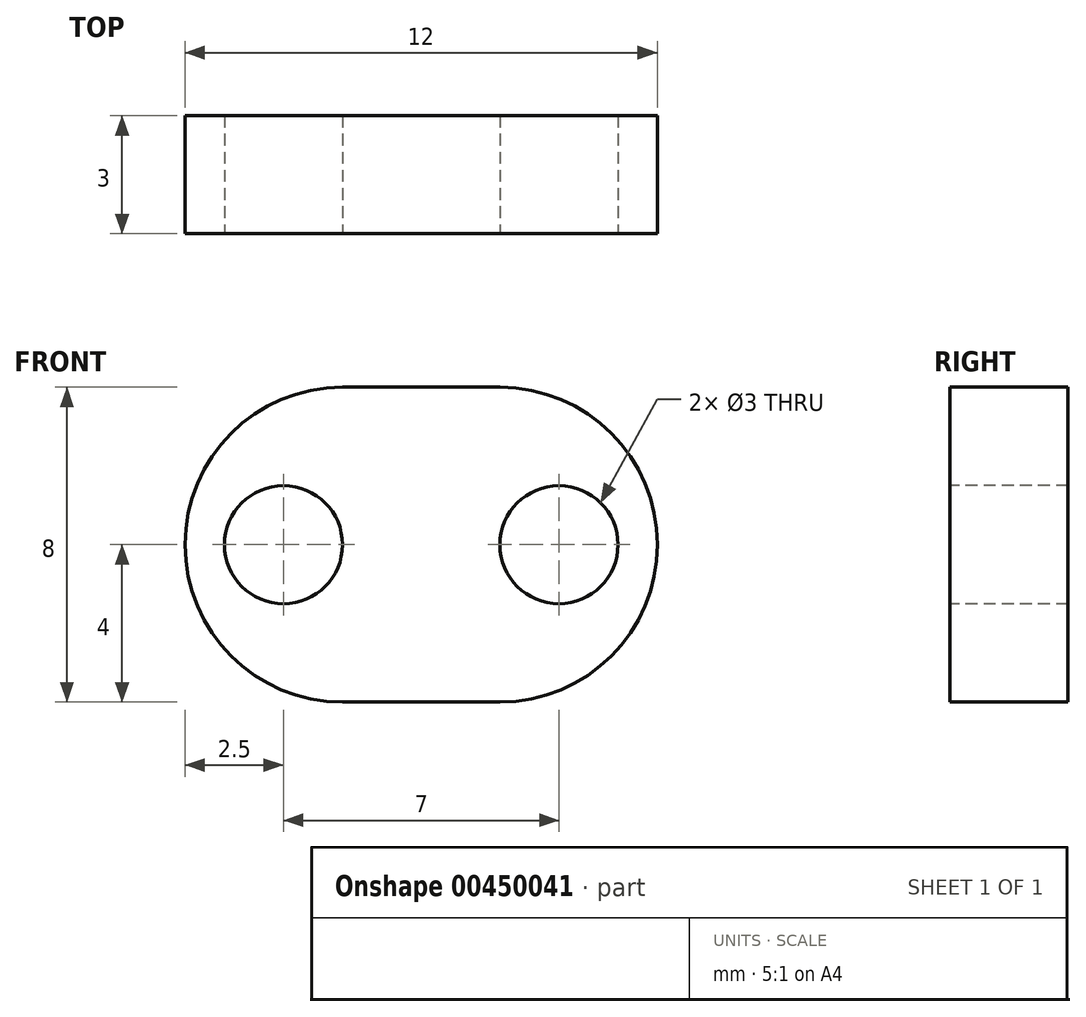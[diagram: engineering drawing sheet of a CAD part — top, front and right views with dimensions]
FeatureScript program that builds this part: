
annotation { "Feature Type Name" : "Feature", "Feature Type Description" : "" }
export const myFeature = defineFeature(function(context is Context, id is Id, definition is map)
    precondition{}
    {
        {
            var Q0;
            Q0=qCreatedBy(makeId("Top.planeOp"),FACE);
            var sketch = newSketch(context, id + "F0", { "sketchPlane" : qUnion([Q0])});
            skLineSegment(sketch, "E0.bottom", {"start": v(6, 1.5) * mm, "end": v(-6, 1.5) * mm});
            skLineSegment(sketch, "E0.top", {"start": v(6, -1.5) * mm, "end": v(-6, -1.5) * mm});
            skLineSegment(sketch, "E0.left", {"start": v(6, 1.5) * mm, "end": v(6, -1.5) * mm});
            skLineSegment(sketch, "E0.right", {"start": v(-6, 1.5) * mm, "end": v(-6, -1.5) * mm});
            skPoint(sketch, "E0.middle", {"position": v(0, 0) * mm});
            skSolve(sketch);
        }
        {
            var Q0;
            Q0 = qSketchRegion(id + "F0", true);
            extrude(context, id + "F1", {"entities" : qUnion([Q0]), "endBound" : BoundingType.SYMMETRIC, "depth" : 8 * mm});
        }
        {
            var Q0;
            Q0=makeQuery(id+"F1.opExtrude","SWEPT_FACE",FACE,{"disambiguationData":[OSD([sQuery(id+"F0.wireOp",EDGE,"E0.top")])]});
            var sketch = newSketch(context, id + "F2", { "sketchPlane" : qUnion([Q0])});
            skCircle(sketch, "E1", {"center": v(-3.5, 0) * mm, "radius": 1.5 * mm});
            skCircle(sketch, "E2.MirrorC", {"center": v(3.5, 0) * mm, "radius": 1.5 * mm});
            skSolve(sketch);
        }
        {
            var Q0;
            Q0 = qSketchRegion(id + "F2", true);
            extrude(context, id + "F3", {"entities" : qUnion([Q0]), "operationType" : NewBodyOperationType.REMOVE, "oppositeDirection" : true, "depth" : 25 * mm});
        }
        {
            var Q0;
            Q0=makeQuery(id+"F1.opExtrude","CAP_EDGE",EDGE,{"disambiguationData":[OSD([sQuery(id+"F0.wireOp",EDGE,"E0.right")])],"isStart":false});
            var Q1;
            Q1=makeQuery(id+"F1.opExtrude","CAP_EDGE",EDGE,{"disambiguationData":[OSD([sQuery(id+"F0.wireOp",EDGE,"E0.right")])],"isStart":true});
            var Q2;
            Q2=makeQuery(id+"F1.opExtrude","CAP_EDGE",EDGE,{"disambiguationData":[OSD([sQuery(id+"F0.wireOp",EDGE,"E0.left")])],"isStart":false});
            var Q3;
            Q3=makeQuery(id+"F1.opExtrude","CAP_EDGE",EDGE,{"disambiguationData":[OSD([sQuery(id+"F0.wireOp",EDGE,"E0.left")])],"isStart":true});
            fillet(context, id + "F4", {"entities" : qUnion([Q0, Q1, Q2, Q3]), "radius" : 4 * mm, "tangentPropagation" : true, "allowEdgeOverflow" : false});
        }
    });
